# Revit family: UnoFloor Light(C)(CI)_RFA_1
name_source: partatom
category: Pipe Accessories
units: mm (PartAtom-declared; Revit-internal decimal feet)

## family parameters
Always vertical = Yes
Cut with Voids When Loaded = No
OmniClass Number = 23.65.55.14.17
OmniClass Title = Adjusting/Controlling Valves for Liquid Services
Part Type = Valve - Breaks Into
Round Connector Dimension = Use Diameter
Shared = No
Work Plane-Based = Yes

## types (3) — shared parameters
Body Material = Danfoss Steel (Zinc Plated and Painted White)
D = 20 mm  [stored 0.0656168 ft]
Default Elevation = 1219.2 mm  [stored 4 ft]
Description = Distribution Units
H = 769 mm  [stored 2.52297 ft]
H1 = 371 mm  [stored 1.21719 ft]
H2 = 182 mm  [stored 0.597113 ft]
IfcExportAs = IfcValveType
L1 = 50 mm  [stored 0.164042 ft]
L2 = 153 mm  [stored 0.501969 ft]
L3 = 184.6 mm  [stored 0.605643 ft]
L4 = 268 mm  [stored 0.879265 ft]
L5 = 268 mm  [stored 0.879265 ft]
Left Assembly = Yes
LookupTableName = Unofloor Light(C)(CI)_Lookup
Manufacturer = Danfoss
Max Differential Pressure = 0.6 bar
Max Medium Temperature = 60 °C
Nominal Pressure = PN 6
Power = 0 VA
Right Assembly = No
URL = https://store.danfoss.com
Voltage = 230 V
W = 79.5 mm  [stored 0.260827 ft]

## per-type parameters (varying)
| type | IfcExportType | Model | Pack Contents | Type number |
| UnoFloor Light CI_4L-12L | Unofloor CI | 088X3734,088X3735,088X3736,088X3737,088X3738,088X3740,088X3742 | Danfoss Icon2™ Master controller 230V, Stainless steel manifold | 3 |
| UnoFloor Light_4L-12L | Unofloor Light | 088X3704,088X3705,088X3706,088X3707,088X3708,088X3710,088X3712 | Stainless steel manifold | 1 |
| UnoFloor Light C_4L-12L | Unofloor Light C | 088X3714,088X3715,088X3716,088X3717,088X3718,088X3720,088X3722 | Danfoss Icon™ Wiring center 230V, Stainless steel manifold | 2 |

note: [stored X ft] marks values corroborated as IEEE doubles in the binary element streams (Revit-internal decimal feet)

## geometry (parser evidence)
native form markers: Sweep x1
no freeform markers — native parametric forms only
